# Revit family: AnchorPoint_Kattsafe_RopeAccess
name_source: partatom
category: Specialty Equipment
units: mm (PartAtom-declared; Revit-internal decimal feet)

## family parameters
Cut with Voids When Loaded = No
Enable Cutting in Views = No
Host = Face
Maintain Annotation Orientation = No
OmniClass Number = 23.27.71.21
Part Type = Normal
Room Calculation Point = No
Round Connector Dimension = Use Diameter
Shared = No

## types (2) — shared parameters
Assembly Code = E1090100
Description = Our Kattsafe anchor points are specifically designed, manufactured, and tested to comply with and often exceed Australian Standards, effectively handling excessive loads and saving lives when using a harness and lanyard system.
ElementType = Fall Protection
Export Type to IFC As = IfcBuildingElementProxy
IfcExportAs = IfcBuildingElementProxy
IfcExportType = USERDEFINED
Manufacturer = Kattsafe®
ManufacturerOverallDepth = 267 mm  [stored 0.875984 ft]
ManufacturerOverallHeight = 70 mm  [stored 0.229659 ft]
ManufacturerOverallWidth = 552 mm  [stored 1.81102 ft]
ManufacturerURLProductSpecific = https://kattsafe.com.au
Material = Steel_Stainless_Kattsafe_Satin
ModifiedIssue = 20240430 $
Type IFC Predefined Type = USERDEFINED
URL = https://kattsafe.com.au
Uniclass2015Code = Pr_40_70_75_75
Uniclass2015Title = Safety access anchor devices
Uniclass2015Version = Products v1.23
zero-valued in all types: Default Elevation

## per-type parameters (varying)
| type | ManufacturerSpecCode | Model | Type Comments |
| Standard (AP141A) | AP141A | AP141A | Top Mount Swivel Rope Access Anchor - Fall arrest 15kN rated - Rope access 12kN - 3.2kg |
| Wide (AP141W) | AP141W | AP141W | Top Mount Swivel Rope Access Anchor - Wide Deck - Suits 300 to 372mm deck - 15kN rated - 2.8kg |

note: [stored X ft] marks values corroborated as IEEE doubles in the binary element streams (Revit-internal decimal feet)

## geometry (parser evidence)
native form markers: Sweep x3
no freeform markers — native parametric forms only
